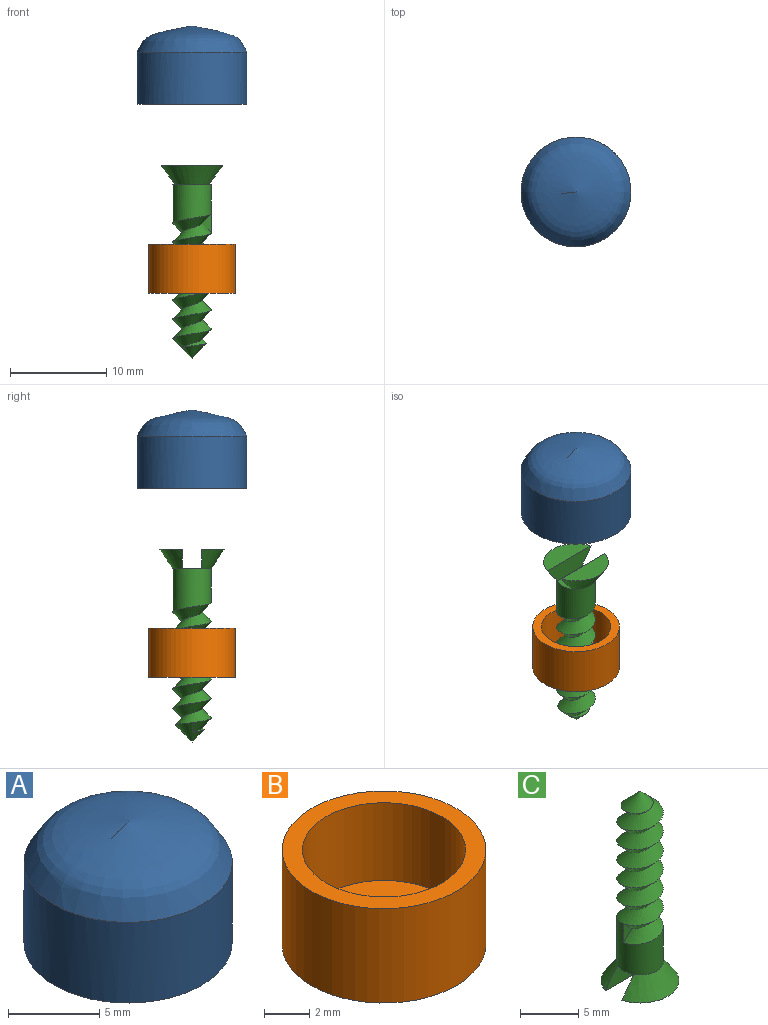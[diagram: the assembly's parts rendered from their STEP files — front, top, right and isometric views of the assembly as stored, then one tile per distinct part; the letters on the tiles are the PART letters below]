
ASSEMBLY  parts=3 mates=2
PART A: 5 faces, bbox 11.4x11.4x8.1 mm
  f0: cylinder r=5.7mm len=11.4mm, axis (0,0,1), area 193.4mm2, adj f1,f4
  f1: plane 11.4x11.4mm, normal (0,0,-1), area 29.7mm2, adj f0,f2
  f2: cylinder r=4.8mm len=9.6mm, axis (0,0,1), area 153.8mm2, adj f1,f3
  f3: cone r=4.8mm half-angle=66.4deg, axis (0,0,-1), area 79mm2, adj f2
  f4: revolved ~11.4x11.4mm, area 132.4mm2, adj f0
PART B: 6 faces, bbox 9x9x5.1 mm
  f0: cylinder r=2.4mm len=4.8mm, axis (0,0,-1), area 13.6mm2, adj f1,f5
  f1: plane 9x9mm, normal (0,0,-1), area 45.5mm2, adj f0,f2
  f2: cylinder r=4.5mm len=9mm, axis (0,0,-1), area 144.2mm2, adj f1,f3
  f3: plane 9x9mm, normal (0,0,1), area 22.9mm2, adj f2,f4
  f4: cylinder r=3.6mm len=7.2mm, axis (0,0,-1), area 95mm2, adj f3,f5
  f5: plane 7.2x7.2mm, normal (0,0,1), area 22.6mm2, adj f0,f4
PART C: 12 faces, bbox 6.6x6.9x20.5 mm
  f0: plane 4x2mm, normal (0,0,-1), area 7.7mm2, adj f1,f5,f7
  f1: cylinder r=2mm len=5mm, axis (0,0,-1), area 50.3mm2, adj f0,f2,f4,f9,f10
  f2: plane 2x1mm, normal (0,-1,0), area 1mm2, adj f1,f3,f4
  f3: bspline ~14.33x4.62mm, area 80.6mm2, adj f2,f4,f11
  f4: bspline ~14.33x4.62mm, area 87.5mm2, adj f1,f2,f3,f11
  f5: plane 6.56x2.16mm, normal (0,-1,0), area 9.9mm2, adj f0,f6,f10
  f6: plane 6.4x2.35mm, normal (0,0,-1), area 11.1mm2, adj f5,f10
  f7: plane 6.56x2.16mm, normal (0,1,0), area 9.9mm2, adj f0,f8,f9
  f8: plane 6.4x2.35mm, normal (0,0,-1), area 11.1mm2, adj f7,f9
  f9: cone r=3.35mm half-angle=34.1deg, axis (0,0,-1), area 15.1mm2, adj f1,f7,f8
  f10: cone r=3.35mm half-angle=34.1deg, axis (0,0,-1), area 15.1mm2, adj f1,f5,f6
  f11: cone r=2mm half-angle=45deg, axis (0,0,-1), area 10.4mm2, adj f3,f4
PLACE A t=(-12.6,0,19.62)mm
PLACE B at identity
PLACE C rot(axis=(0,1,0),180deg) t=(0,0,11.28)mm
MATE slider C.f1 <-> B.f0  axis (0,0,1) through (0,0,8.76)mm
MATE slider B.f0 <-> A.f0  axis (0,0,1) through (0,0,5.1)mm
